# Revit family: sicompact_r__31_maxi___pl32_5xa7592e1k22_b9d3
name_source: partatom
category: Lighting Fixtures
units: mm (PartAtom-declared; Revit-internal decimal feet)

## family parameters
Cut with Voids When Loaded = No
Host = Face
Light Source = No
Part Type = Normal
Room Calculation Point = No
Round Connector Dimension = Use Diameter
Shared = No

## types (1)
- SiCompact® 31 maxi  PL32 (1 x LED, 65000 lm, 490 W, 3000K)
    Apparent Load = 490 VA
    CIE Flux Codes = 32 77 99 100 100
    Color Rendering = 70
    Color Temperature = 3000K
    Default Elevation = 1800 mm
    Description = SiCompact® 31 maxi, floodlight, primary light control with lens, of plastic, of toughened safety glass, transparent, light distribution: PL32, light emission: direct distribution, primary light characteristic: asymmetric, installation type: surface-mounted, LED, High Power LED, rated luminous flux: 65.000lm, luminous efficacy: 133lm/W, light colour: 730, colour temperature: 3000K, control gear: DALI, with terminal, 5-pole, mains connection: 220..240V, AC, 50/60Hz, rated input power: 490W, of diecast aluminium, powder-coated, metallic grey (RAL 9006), length: 790mm, width: 560mm, height: 85mm, bracket, of sheet steel, powder-coated, metallic grey (RAL 9006), protection rating (complete): IP66, insulation class (complete): insulation class I (protective earthing), certification: CE, ENEC, impact resistance: IK08, permissible operating ambient temperature: -30..+35°C, permissible operating ambient temperature for outdoor applications: -30..+45°C, permissible storage temperature: -30..+65°C, packaging unit: 1 piece

Light Distribution: PL32
    Height = 80 mm  [stored 0.262467 ft]
    Lamp = 1 x LED
    Lamp Light Flux = 65000 lm
    Lamp Power = 490 W
    Lamp count = 1
    Length = 769 mm
    Luminous efficacy = 133 lm/W
    Manufacturer = Siteco
    ModVariant = No
    Model = 5XA7592E1K22
    Mounting Place = Wall
    Mounting Type = Surface mounted
    Number of Poles = 1
    OnlyDefault = Yes
    Power Factor = 1
    Product Name = SiCompact® 31 maxi | PL32
    Product group = floodlight | wall mounted
    ProductGroupID = 2001
    Protection Class = Protection class I
    Protection Degree = IP 66
    RLX_Detail_Level = 1
    RLX_Emergency_Light_Flux = 0 lm
    RLX_Emergency_Type = 0
    RLX_Emergency_Type_DB = No
    RlxData = <blob elided: 76625 chars, md5=3bd437ff>
    Socket = socket
    Standby Power = 0 W
    System Light Flux = 65000 lm
    System Power = 490 W
    Type Comments = Product without accessories
    Type Image = l_1003756.jpg
    URL = http://relux.com
    VarID = ---
    Voltage = 0 V
    Weight = 0.00 kg
    Width = 560 mm

note: [stored X ft] marks values corroborated as IEEE doubles in the binary element streams (Revit-internal decimal feet)

## geometry (parser evidence)
native form markers: Sweep x10
no freeform markers — native parametric forms only
